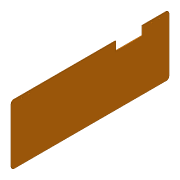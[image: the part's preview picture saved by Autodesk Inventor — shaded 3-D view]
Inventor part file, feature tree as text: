
AUTODESK INVENTOR PART (.ipt)
format: ipt  version: 2016 (Build 200138000, 138)  size: 137,728 bytes
history: native  units: in
note: dims shown in document units (in); Inventor stores cm internally (conversion verified against a paired STEP export)
features: extrude x3, sketch x3, fillet x2
ambient origin geometry x8: Origin, YZ Plane, XZ Plane, XY Plane, X Axis, Y Axis, Z Axis, Center Point
bodies: Body1 (feature_tree)
feature tree (8):
  extrude  "Extrusion2"  Depth=23.7in
  fillet  "Fillet1"  Radius=0.1125in
  fillet  "Fillet2"  Radius=0.4in
  extrude  "Extrusion3"  Depth=0.0225in TaperAngle=0.0deg
  extrude  "Extrusion5"  Depth=4.0in
  sketch  "Sketch1"  dims[d3=9.0in d4=23.7in d5=0.1125in d6=0.0in d7=0.4in]
  sketch  "Sketch3"  dims[d8=0.0225in d19=0.2in d20=0.0in]
  sketch  "Sketch4"  dims[d48=4.0in d49=4.0in d50=0.0in d52=0.2in d53=0.3in d54=1.1in d55=1.5in d58=1.1in d60=1.5in d61=1.1in d62=0.0in d63=0.4477in d64=1.309in]
